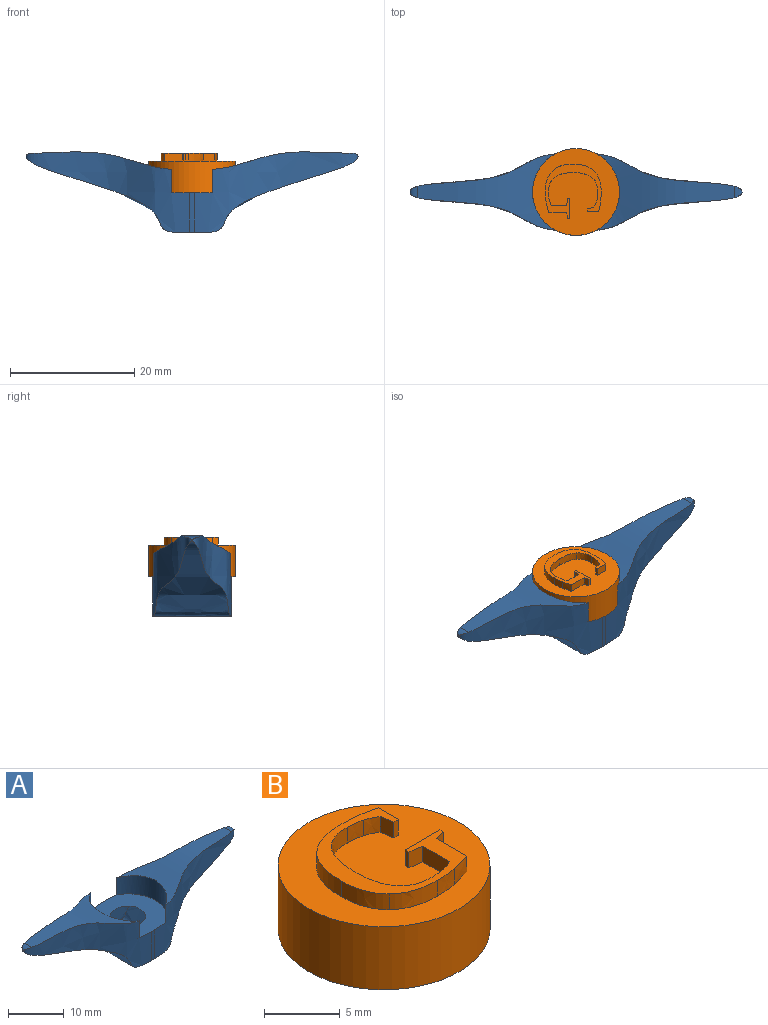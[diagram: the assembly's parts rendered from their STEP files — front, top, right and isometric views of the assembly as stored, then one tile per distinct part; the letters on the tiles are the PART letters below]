
ASSEMBLY  parts=2 mates=1
PART A: 17 faces, bbox 66.1x25.4x25.6 mm
  f0: extruded ~22.07x12.28mm, area 96.5mm2, adj f1,f2,f3,f4
  f1: extruded ~26.3x12.91mm, area 144mm2, adj f0,f2,f4,f5,f6,f7
  f2: extruded ~24.04x12.7mm, area 176.1mm2, adj f0,f1,f3,f6,f8,f9
  f3: extruded ~26.3x12.91mm, area 144mm2, adj f0,f2,f4,f5,f8,f10
  f4: cylinder r=6.99mm len=12.28mm, axis (0,0,-1), area 56.1mm2, adj f0,f1,f3,f5
  f5: plane 26.67x25.4mm, normal (0,0,1), area 115.8mm2, adj f1,f3,f4,f7,f10,f11,f12,f13
  f6: plane 17.99x17.29mm, normal (0,0,-1), area 18.7mm2, adj f1,f2,f7,f9,f12,f15
  f7: cylinder r=6.35mm len=6.35mm, axis (0,0,-1), area 4.9mm2, adj f1,f5,f6,f12
  f8: plane 5.3x4.59mm, normal (0,0,-1), area 18.7mm2, adj f2,f3,f9,f10,f14,f15
  f9: cylinder r=3.17mm len=5.82mm, axis (0,0,-1), area 0mm2, adj f2,f6,f8,f15
  f10: cylinder r=6.35mm len=6.35mm, axis (0,0,-1), area 4.9mm2, adj f3,f5,f8,f14
  f11: cylinder r=3.17mm len=1.02mm, axis (0,0,-1), area 0mm2, adj f5
  f12: extruded ~26.3x12.92mm, area 143.8mm2, adj f5,f6,f7,f13,f15,f16
  f13: cylinder r=6.99mm len=12.28mm, axis (0,0,-1), area 56.1mm2, adj f5,f12,f14,f16
  f14: extruded ~26.3x12.92mm, area 143.8mm2, adj f5,f8,f10,f13,f15,f16
  f15: extruded ~24.04x12.7mm, area 173.8mm2, adj f6,f8,f9,f12,f14,f16
  f16: extruded ~22.07x12.28mm, area 96.5mm2, adj f12,f13,f14,f15
PART B: 30 faces, bbox 14x14x6.4 mm
  f0: cylinder r=6.99mm len=13.97mm, axis (0,0,-1), area 223mm2, adj f1,f28
  f1: plane 13.97x13.97mm, normal (0,0,-1), area 107.7mm2, adj f0,f2
  f2: sphere r=3.81mm, area 91.2mm2, adj f1
  f3: extruded ~1.76x1.27mm, area 2.3mm2, adj f4,f27,f28,f29
  f4: extruded ~3.33x1.27mm, area 4.6mm2, adj f3,f5,f28,f29
  f5: extruded ~3.27x1.27mm, area 4.5mm2, adj f4,f6,f28,f29
  f6: extruded ~3.45x1.27mm, area 4.7mm2, adj f5,f7,f28,f29
  f7: extruded ~3.39x1.27mm, area 4.7mm2, adj f6,f8,f28,f29
  f8: extruded ~3.08x1.27mm, area 4mm2, adj f7,f9,f28,f29
  f9: plane 1.89x1.27mm, normal (1,0,0), area 2.4mm2, adj f8,f10,f28,f29
  f10: plane 1.27x0.44mm, normal (0,-1,0), area 0.6mm2, adj f9,f11,f28,f29
  f11: plane 1.27x1.09mm, normal (-0.99,-0.16,0), area 1.4mm2, adj f10,f12,f28,f29
  f12: extruded ~1.27x1.08mm, area 1.5mm2, adj f11,f13,f28,f29
  f13: extruded ~1.33x1.27mm, area 1.7mm2, adj f12,f14,f28,f29
  f14: extruded ~2.45x1.27mm, area 3.5mm2, adj f13,f15,f28,f29
  f15: extruded ~3.05x1.27mm, area 4.1mm2, adj f14,f16,f28,f29
  f16: extruded ~2.93x1.27mm, area 3.9mm2, adj f15,f17,f28,f29
  f17: extruded ~2.36x1.27mm, area 3.4mm2, adj f16,f18,f28,f29
  f18: extruded ~1.27x1.15mm, area 1.5mm2, adj f17,f19,f28,f29
  f19: extruded ~1.27x0.92mm, area 1.2mm2, adj f18,f20,f28,f29
  f20: plane 2.49x1.27mm, normal (-1,0,0), area 3.2mm2, adj f19,f21,f28,f29
  f21: plane 1.27x1.13mm, normal (-0.15,-0.99,0), area 1.4mm2, adj f20,f22,f28,f29
  f22: plane 1.27x0.35mm, normal (-1,0,0), area 0.4mm2, adj f21,f23,f28,f29
  f23: plane 3.24x1.27mm, normal (0,1,0), area 4.1mm2, adj f22,f24,f28,f29
  f24: plane 1.27x0.35mm, normal (1,0,0), area 0.4mm2, adj f23,f25,f28,f29
  f25: plane 1.27x0.86mm, normal (0.2,-0.98,0), area 1.1mm2, adj f24,f26,f28,f29
  f26: plane 2.85x1.27mm, normal (1,0,0), area 3.6mm2, adj f25,f27,f28,f29
  f27: extruded ~1.58x1.27mm, area 2.1mm2, adj f3,f26,f28,f29
  f28: plane 13.97x13.97mm, normal (0,0,1), area 131.4mm2, adj f0,f3,f4,f5,f6,f7,f8,f9
  f29: plane 9.01x8.71mm, normal (0,0,1), area 21.9mm2, adj f3,f4,f5,f6,f7,f8,f9,f10
PLACE A t=(-3.93,6.81,0)mm
PLACE B rot(axis=(0,0,-1),90deg) t=(-3.93,6.81,6.35)mm
MATE planar B.f0 <-> A.f5  axis (0,0,-1) through (-3.93,6.81,6.35)mm
